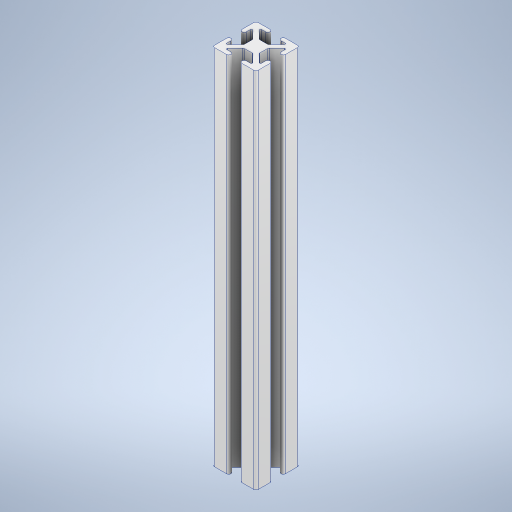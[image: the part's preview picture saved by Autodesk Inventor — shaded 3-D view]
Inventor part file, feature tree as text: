
AUTODESK INVENTOR PART (.ipt)
format: ipt  version: 2024 (Build 280153000, 153)  size: 349,184 bytes
history: native  units: in
note: dims shown in document units (in); Inventor stores cm internally (conversion verified against a paired STEP export)
features: fillet x2, extrude x1, sketch x1
ambient origin geometry x8: Origin, YZ Plane, XZ Plane, XY Plane, X Axis, Y Axis, Z Axis, Center Point
bodies: Solid1 (feature_tree)
feature tree (4):
  extrude  "Extrusion1"  Depth=1.0in
  fillet  "Fillet1"  Radius=0.8in
  fillet  "Fillet2"  Radius=0.8in
  sketch  "Sketch1"  dims[d0=1.0in d1=1.0in d2=0.8in d3=0.8in d4=0.35in d5=0.35in d6=0.125in d7=0.25in d8=0.125in d9=0.25in d10=0.1in d11=0.1in d12=8.35in d13=0.0in d14=0.05in d15=0.025in]
